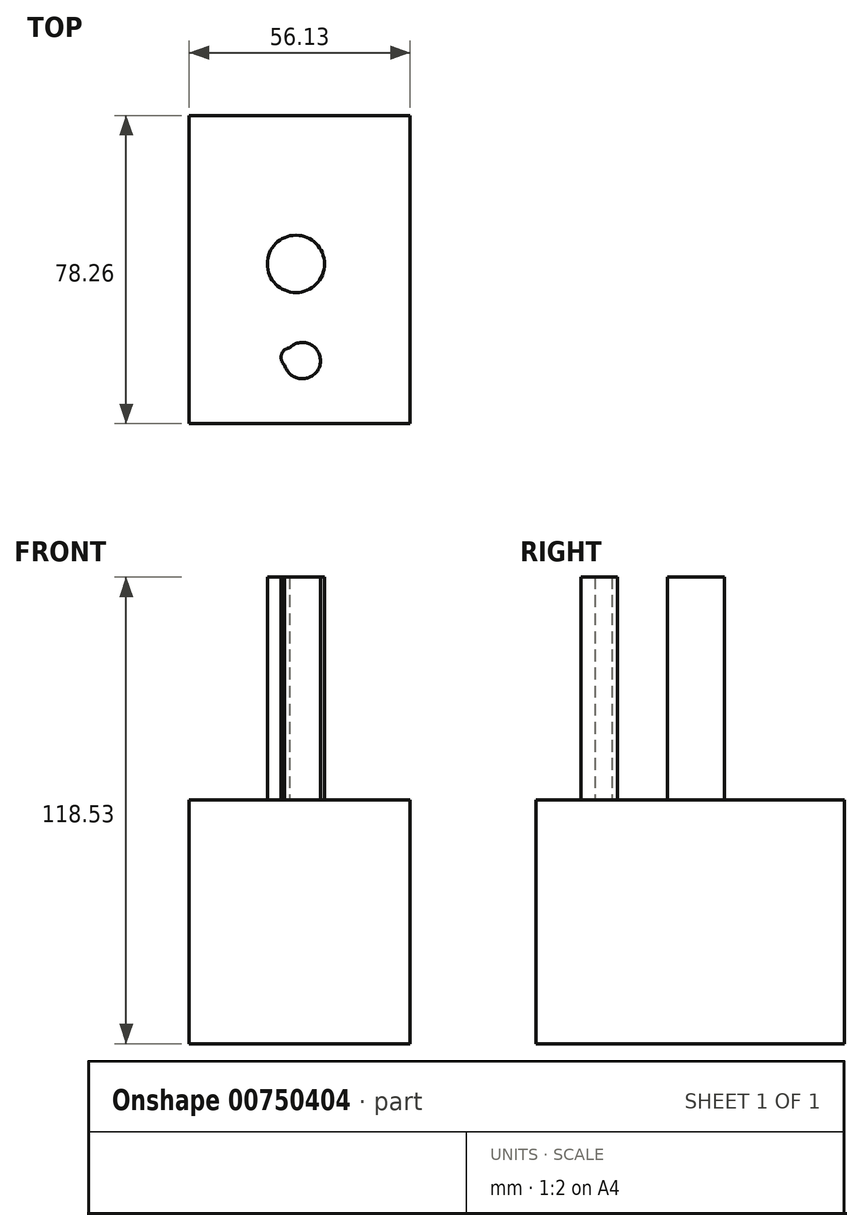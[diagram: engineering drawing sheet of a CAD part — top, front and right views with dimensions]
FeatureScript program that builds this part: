
annotation { "Feature Type Name" : "Feature", "Feature Type Description" : "" }
export const myFeature = defineFeature(function(context is Context, id is Id, definition is map)
    precondition{}
    {
        {
            var Q0;
            Q0=qCreatedBy(makeId("Right.planeOp"),FACE);
            var sketch = newSketch(context, id + "F0", { "sketchPlane" : qUnion([Q0])});
            skLineSegment(sketch, "E0.bottom", {"start": v(0, 0) * mm, "end": v(78.26, 0) * mm});
            skLineSegment(sketch, "E0.top", {"start": v(0, -61.89) * mm, "end": v(78.26, -61.89) * mm});
            skLineSegment(sketch, "E0.left", {"start": v(0, 0) * mm, "end": v(0, -61.89) * mm});
            skLineSegment(sketch, "E0.right", {"start": v(78.26, 0) * mm, "end": v(78.26, -61.89) * mm});
            skSolve(sketch);
        }
        {
            var Q0;
            Q0 = qSketchRegion(id + "F0", true);
            extrude(context, id + "F1", {"entities" : qUnion([Q0]), "depth" : 56.13 * mm, "offsetDistance" : 25.4 * mm});
        }
        {
            var Q0;
            Q0=makeQuery(id+"F1.opExtrude","CAP_FACE",FACE,{"disambiguationData":[OSD([sQuery(id+"F0.wireOp",EDGE,"E0.bottom"),sQuery(id+"F0.wireOp",EDGE,"E0.top"),sQuery(id+"F0.wireOp",EDGE,"E0.left"),sQuery(id+"F0.wireOp",EDGE,"E0.right")])],"isStart":false});
            var sketch = newSketch(context, id + "F2", { "sketchPlane" : qUnion([Q0])});
            skCircle(sketch, "E1", {"center": v(40.3, -31.44) * mm, "radius": 10.83 * mm});
            skCircle(sketch, "E2", {"center": v(15.83, -35.85) * mm, "radius": 11.31 * mm});
            skSolve(sketch);
        }
        {
            var Q0;
            Q0=sQuery(id+"F2.wireOp",EDGE,"E1");
            var Q1;
            Q1=sQuery(id+"F2.wireOp",EDGE,"E2");
            extrude(context, id + "F3", {"bodyType" : ToolBodyType.SURFACE, "surfaceEntities" : qUnion([Q0, Q1]), "endBound" : BoundingType.SYMMETRIC, "oppositeDirection" : true, "depth" : 287.02 * mm, "offsetDistance" : 25.4 * mm});
        }
        {
            var Q0;
            Q0=makeQuery(id+"F1.opExtrude","SWEPT_FACE",FACE,{"disambiguationData":[OSD([sQuery(id+"F0.wireOp",EDGE,"E0.bottom")])]});
            var sketch = newSketch(context, id + "F4", { "sketchPlane" : qUnion([Q0])});
            skCircle(sketch, "E3", {"center": v(27.1, 40.6) * mm, "radius": 7.27 * mm});
            skCircle(sketch, "E4", {"center": v(25.75, 16.83) * mm, "radius": 2.45 * mm});
            skCircle(sketch, "E5", {"center": v(28.72, 16.02) * mm, "radius": 4.61 * mm});
            skSolve(sketch);
        }
        {
            var Q0;
            Q0 = qSketchRegion(id + "F4", true);
            extrude(context, id + "F5", {"entities" : qUnion([Q0]), "operationType" : NewBodyOperationType.ADD, "depth" : 56.64 * mm, "offsetDistance" : 25.4 * mm});
        }
    });
